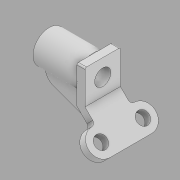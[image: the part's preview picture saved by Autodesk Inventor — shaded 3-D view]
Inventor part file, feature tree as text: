
AUTODESK INVENTOR PART (.ipt)
format: ipt  version: 2020 (Build 240168000, 168)  size: 203,264 bytes
history: native  units: mm
features: sketch x6, projected_geometry x4, extrude x3, other x2, hole x2, fillet x2
ambient origin geometry x8: Origin, YZ Plane, XZ Plane, XY Plane, X Axis, Y Axis, Z Axis, Center Point
bodies: Body1 (feature_tree)
feature tree (19):
  other  "Sólido1"
  extrude  "Extrusión1"  Depth=35.0mm
  extrude  "Extrusión2"  Depth=25.0mm
  extrude  "Extrusión3"  TaperAngle=45.0deg  [1 undecoded]
  other  "Nervio1"
  hole  "Agujero1"  [1 undecoded]
  hole  "Agujero2"  [1 undecoded]
  fillet  "Empalme1"  Radius=83.0mm
  fillet  "Empalme2"  Radius=41.5mm
  sketch  "Boceto1"  dims[d0=16.0mm d3=35.0mm]
  sketch  "Boceto2"  dims[d5=25.0mm d6=25.0mm]
  projected_geometry  "Contorno proyectado1"
  sketch  "Boceto3"  dims[d7=70.0mm d10=45.0deg]
  sketch  "Boceto4"  dims[d11=0.0mm d12=70.0mm d13=0.0mm]
  projected_geometry  "Contorno proyectado2"
  projected_geometry  "Contorno proyectado3"
  projected_geometry  "Contorno proyectado4"
  sketch  "Boceto5"  dims[d14=64.0mm d15=106.0mm d16=0.0mm d17=83.0mm d18=41.5mm]
  sketch  "Boceto6"  dims[d19=25.0mm d20=10.0mm d21=0.0mm d22=25.0mm d23=7.0mm d24=1.0mm d25=16.0mm d26=0.0mm d27=0.0mm d28=1.0mm d29=1.0mm d30=32.0mm d31=6.0mm d32=38.1mm d33=2.54mm d34=90.0deg d35=38.1mm d36=0.0mm d37=25.0mm d38=6.0mm d39=38.1mm d40=2.54mm d41=90.0deg d42=38.1mm d43=0.0mm d44=45.0deg d45=3.0mm d46=32.0mm d47=7.0mm]
note: 3 required parameter values undecoded (feature->parameter linkage not recoverable at this tier; creation-order binding heuristic only, values carry confidence <= 0.55)
